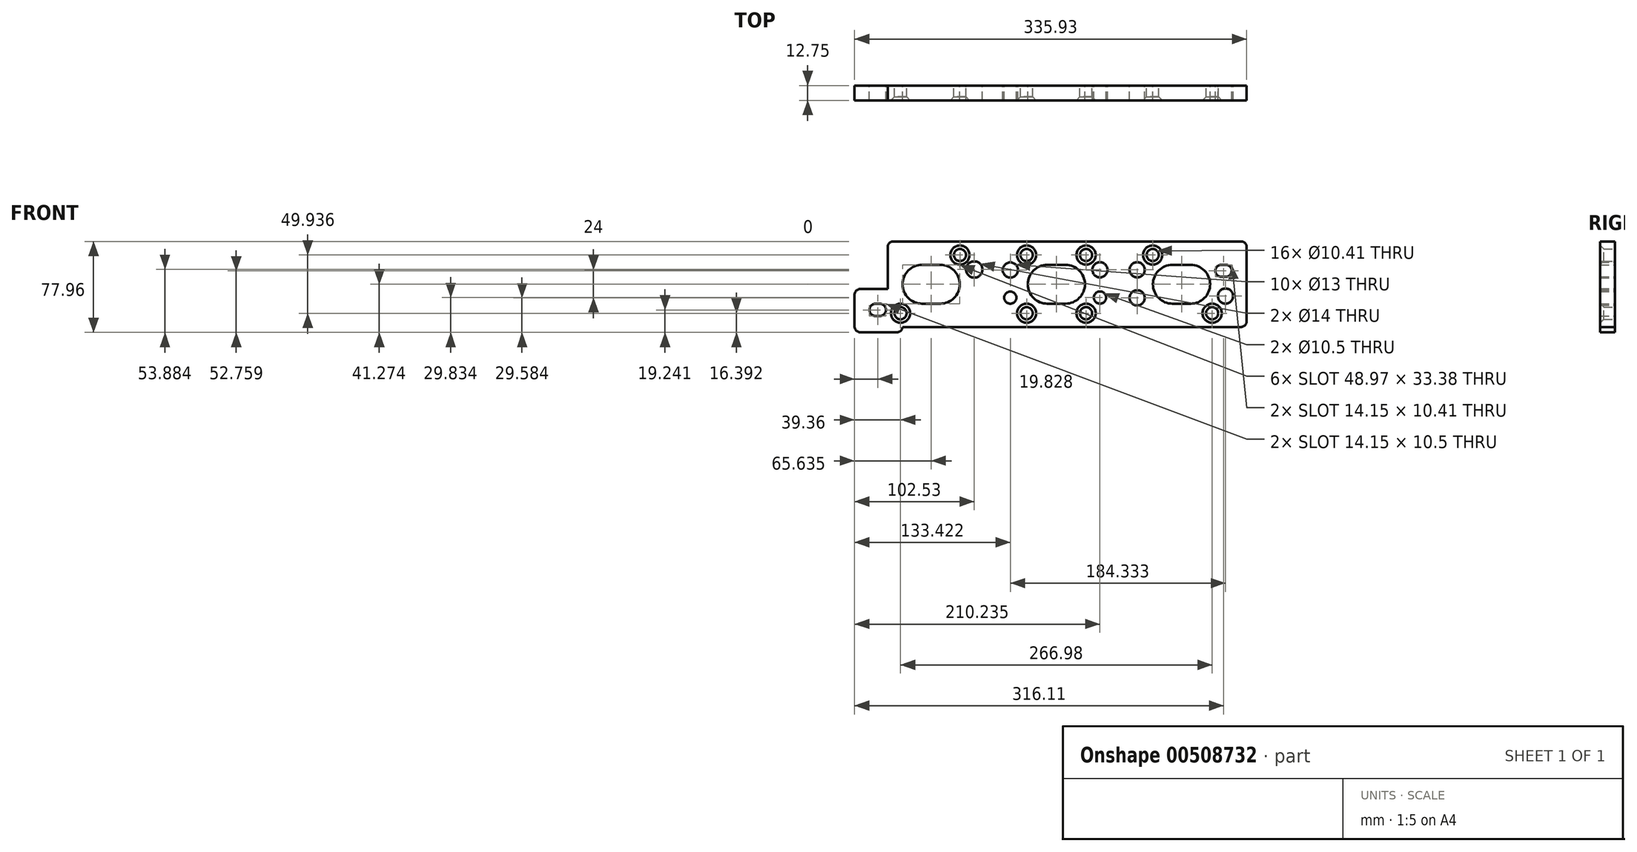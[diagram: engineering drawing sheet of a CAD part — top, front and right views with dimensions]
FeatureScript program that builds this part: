
annotation { "Feature Type Name" : "Feature", "Feature Type Description" : "" }
export const myFeature = defineFeature(function(context is Context, id is Id, definition is map)
    precondition{}
    {
        {
            var Q0;
            Q0=qCreatedBy(makeId("Front.planeOp"),FACE);
            var sketch = newSketch(context, id + "F0", { "sketchPlane" : qUnion([Q0])});
            skLineSegment(sketch, "E0", {"start": v(-7.76, 16.6) * mm, "end": v(7.83, 16.6) * mm});
            skArc(sketch, "E1", {"start": v(7.83, -16.78) * mm, "mid": v(24.52, -0.09) * mm, "end": v(7.83, 16.6) * mm});
            skLineSegment(sketch, "E2", {"start": v(7.83, -16.78) * mm, "end": v(-7.76, -16.78) * mm});
            skArc(sketch, "E3", {"start": v(-7.76, 16.6) * mm, "mid": v(-24.45, -0.09) * mm, "end": v(-7.76, -16.78) * mm});
            skPoint(sketch, "E4", {"position": v(-24.45, -0.09) * mm});
            skPoint(sketch, "E5", {"position": v(24.52, -0.09) * mm});
            skLineSegment(sketch, "E6", {"start": v(99.45, 16.6) * mm, "end": v(115.04, 16.6) * mm});
            skArc(sketch, "E7", {"start": v(115.04, -16.78) * mm, "mid": v(131.73, -0.09) * mm, "end": v(115.04, 16.6) * mm});
            skLineSegment(sketch, "E8", {"start": v(115.04, -16.78) * mm, "end": v(99.45, -16.78) * mm});
            skArc(sketch, "E9", {"start": v(99.45, 16.6) * mm, "mid": v(82.76, -0.09) * mm, "end": v(99.45, -16.78) * mm});
            skPoint(sketch, "E10", {"position": v(82.76, -0.09) * mm});
            skPoint(sketch, "E11", {"position": v(131.73, -0.09) * mm});
            skLineSegment(sketch, "E12", {"start": v(206.7, 16.6) * mm, "end": v(222.3, 16.6) * mm});
            skArc(sketch, "E13", {"start": v(222.3, -16.78) * mm, "mid": v(238.99, -0.09) * mm, "end": v(222.3, 16.6) * mm});
            skLineSegment(sketch, "E14", {"start": v(222.3, -16.78) * mm, "end": v(206.7, -16.78) * mm});
            skArc(sketch, "E15", {"start": v(206.7, 16.6) * mm, "mid": v(190.02, -0.09) * mm, "end": v(206.7, -16.78) * mm});
            skPoint(sketch, "E16", {"position": v(190.01, -0.09) * mm});
            skPoint(sketch, "E17", {"position": v(238.99, -0.09) * mm});
            skPoint(sketch, "E18", {"position": v(107.25, 0) * mm});
            skPoint(sketch, "E19", {"position": v(214.5, 0) * mm});
            skCircle(sketch, "E20", {"center": v(36.93, 12.52) * mm, "radius": 7 * mm});
            skCircle(sketch, "E21", {"center": v(67.82, 12.16) * mm, "radius": 6.5 * mm});
            skCircle(sketch, "E22", {"center": v(67.82, -11.58) * mm, "radius": 5.2 * mm});
            skPoint(sketch, "E23", {"position": v(67.82, -16.78) * mm});
            skLineSegment(sketch, "E24", {"start": v(-47.6, -16.87) * mm, "end": v(-43.95, -16.87) * mm});
            skArc(sketch, "E25", {"start": v(-43.95, -27.37) * mm, "mid": v(-38.7, -22.12) * mm, "end": v(-43.95, -16.87) * mm});
            skLineSegment(sketch, "E26", {"start": v(-43.95, -27.37) * mm, "end": v(-47.6, -27.37) * mm});
            skArc(sketch, "E27", {"start": v(-47.6, -16.87) * mm, "mid": v(-52.85, -22.12) * mm, "end": v(-47.6, -27.37) * mm});
            skPoint(sketch, "E28", {"position": v(-38.7, -22.12) * mm});
            skPoint(sketch, "E29", {"position": v(-52.85, -22.12) * mm});
            skCircle(sketch, "E30", {"center": v(144.63, 12.22) * mm, "radius": 6.5 * mm});
            skCircle(sketch, "E31", {"center": v(144.63, -11.53) * mm, "radius": 5.25 * mm});
            skPoint(sketch, "E32", {"position": v(144.63, -16.78) * mm});
            skPoint(sketch, "E33", {"position": v(138.13, 12.22) * mm});
            skCircle(sketch, "E34", {"center": v(176.51, 12.22) * mm, "radius": 6.5 * mm});
            skCircle(sketch, "E35", {"center": v(176.51, -11.78) * mm, "radius": 6.5 * mm});
            skPoint(sketch, "E36", {"position": v(183.01, 12.22) * mm});
            skLineSegment(sketch, "E37", {"start": v(248.64, 16.6) * mm, "end": v(252.38, 16.6) * mm});
            skArc(sketch, "E38", {"start": v(252.38, 6.2) * mm, "mid": v(257.59, 11.4) * mm, "end": v(252.38, 16.6) * mm});
            skLineSegment(sketch, "E39", {"start": v(252.38, 6.2) * mm, "end": v(248.64, 6.2) * mm});
            skArc(sketch, "E40", {"start": v(248.64, 16.6) * mm, "mid": v(243.44, 11.4) * mm, "end": v(248.64, 6.2) * mm});
            skPoint(sketch, "E41", {"position": v(243.44, 11.4) * mm});
            skPoint(sketch, "E42", {"position": v(257.59, 11.4) * mm});
            skCircle(sketch, "E43", {"center": v(252.16, -10.28) * mm, "radius": 6.5 * mm});
            skPoint(sketch, "E44", {"position": v(252.16, -16.78) * mm});
            skPoint(sketch, "E45", {"position": v(245.65, -10.28) * mm});
            skSolve(sketch);
        }
        {
            var Q0;
            Q0=qCreatedBy(makeId("Front.planeOp"),FACE);
            var sketch = newSketch(context, id + "F1", { "sketchPlane" : qUnion([Q0])});
            skLineSegment(sketch, "E46", {"start": v(-37.2, 36.6) * mm, "end": v(270.33, 36.6) * mm});
            skLineSegment(sketch, "E47", {"start": v(270.33, 36.6) * mm, "end": v(270.33, -36.78) * mm});
            skLineSegment(sketch, "E48", {"start": v(270.33, -36.78) * mm, "end": v(-24.45, -36.78) * mm});
            skLineSegment(sketch, "E49", {"start": v(-24.45, -36.78) * mm, "end": v(-24.45, -41.36) * mm});
            skLineSegment(sketch, "E50", {"start": v(-24.45, -41.36) * mm, "end": v(-65.6, -41.36) * mm});
            skLineSegment(sketch, "E51", {"start": v(-65.6, -41.36) * mm, "end": v(-65.6, -4.12) * mm});
            skLineSegment(sketch, "E52", {"start": v(-65.6, -4.12) * mm, "end": v(-37.2, -4.12) * mm});
            skLineSegment(sketch, "E53", {"start": v(-37.2, -4.12) * mm, "end": v(-37.2, 36.6) * mm});
            skLineSegment(sketch, "E54", {"start": v(-37.2, 36.6) * mm, "end": v(-37.2, 36.6) * mm});
            skSolve(sketch);
        }
        {
            var Q0;
            Q0 = qSketchRegion(id + "F1", true);
            extrude(context, id + "F2", {"entities" : qUnion([Q0]), "depth" : 12.75 * mm});
        }
        {
            var Q0;
            Q0 = qSketchRegion(id + "F0", true);
            extrude(context, id + "F3", {"entities" : qUnion([Q0]), "operationType" : NewBodyOperationType.REMOVE, "depth" : 25 * mm});
        }
        {
            var Q0;
            Q0=makeQuery(id+"F2.opExtrude","SWEPT_EDGE",EDGE,{"disambiguationData":[OSD([sQuery(id+"F1.wireOp",EDGE,"E46"),sQuery(id+"F1.wireOp",EDGE,"E53")])]});
            var Q1;
            Q1=makeQuery(id+"F2.opExtrude","SWEPT_EDGE",EDGE,{"disambiguationData":[OSD([sQuery(id+"F1.wireOp",EDGE,"E51"),sQuery(id+"F1.wireOp",EDGE,"E52")])]});
            var Q2;
            Q2=makeQuery(id+"F2.opExtrude","SWEPT_EDGE",EDGE,{"disambiguationData":[OSD([sQuery(id+"F1.wireOp",EDGE,"E50"),sQuery(id+"F1.wireOp",EDGE,"E51")])]});
            var Q3;
            Q3=makeQuery(id+"F2.opExtrude","SWEPT_EDGE",EDGE,{"disambiguationData":[OSD([sQuery(id+"F1.wireOp",EDGE,"E49"),sQuery(id+"F1.wireOp",EDGE,"E50")])]});
            var Q4;
            Q4=makeQuery(id+"F2.opExtrude","SWEPT_EDGE",EDGE,{"disambiguationData":[OSD([sQuery(id+"F1.wireOp",EDGE,"E46"),sQuery(id+"F1.wireOp",EDGE,"E47")])]});
            var Q5;
            Q5=makeQuery(id+"F2.opExtrude","SWEPT_EDGE",EDGE,{"disambiguationData":[OSD([sQuery(id+"F1.wireOp",EDGE,"E47"),sQuery(id+"F1.wireOp",EDGE,"E48")])]});
            fillet(context, id + "F4", {"entities" : qUnion([Q0, Q1, Q2, Q3, Q4, Q5]), "radius" : 5 * mm, "tangentPropagation" : true, "allowEdgeOverflow" : false});
        }
        {
            var Q0;
            Q0=qCreatedBy(makeId("Front.planeOp"),FACE);
            var sketch = newSketch(context, id + "F5", { "sketchPlane" : qUnion([Q0])});
            skCircle(sketch, "E55", {"center": v(132.71, 24.97) * mm, "radius": 5.2 * mm});
            skCircle(sketch, "E56", {"center": v(132.71, -24.97) * mm, "radius": 5.2 * mm});
            skCircle(sketch, "E57", {"center": v(81.79, -24.97) * mm, "radius": 5.2 * mm});
            skCircle(sketch, "E58", {"center": v(81.79, 24.97) * mm, "radius": 5.2 * mm});
            skCircle(sketch, "E59", {"center": v(240.74, -24.97) * mm, "radius": 5.2 * mm});
            skCircle(sketch, "E60", {"center": v(-26.24, -24.97) * mm, "radius": 5.2 * mm});
            skCircle(sketch, "E61", {"center": v(24.69, 24.97) * mm, "radius": 5.2 * mm});
            skCircle(sketch, "E62", {"center": v(189.81, 24.97) * mm, "radius": 5.2 * mm});
            skSolve(sketch);
        }
        {
            var Q0;
            Q0 = qSketchRegion(id + "F5", true);
            extrude(context, id + "F6", {"entities" : qUnion([Q0]), "operationType" : NewBodyOperationType.REMOVE, "depth" : 25 * mm});
        }
        {
            var Q0;
            Q0=makeQuery(id+"F6.boolean.opBoolean","INTERSECT",EDGE,{"derivedFrom":[makeQuery(id+"F2.opExtrude","CAP_FACE",FACE,{"disambiguationData":[OSD([sQuery(id+"F1.wireOp",EDGE,"E46"),sQuery(id+"F1.wireOp",EDGE,"E47"),sQuery(id+"F1.wireOp",EDGE,"E48"),sQuery(id+"F1.wireOp",EDGE,"E49"),sQuery(id+"F1.wireOp",EDGE,"E50"),sQuery(id+"F1.wireOp",EDGE,"E51"),sQuery(id+"F1.wireOp",EDGE,"E52"),sQuery(id+"F1.wireOp",EDGE,"E53")])],"isStart":false}),makeQuery(id+"F6.opExtrude","SWEPT_FACE",FACE,{"disambiguationData":[OSD([sQuery(id+"F5.wireOp",EDGE,"E61")])]})]});
            var Q1;
            Q1=makeQuery(id+"F6.boolean.opBoolean","INTERSECT",EDGE,{"derivedFrom":[makeQuery(id+"F2.opExtrude","CAP_FACE",FACE,{"disambiguationData":[OSD([sQuery(id+"F1.wireOp",EDGE,"E46"),sQuery(id+"F1.wireOp",EDGE,"E47"),sQuery(id+"F1.wireOp",EDGE,"E48"),sQuery(id+"F1.wireOp",EDGE,"E49"),sQuery(id+"F1.wireOp",EDGE,"E50"),sQuery(id+"F1.wireOp",EDGE,"E51"),sQuery(id+"F1.wireOp",EDGE,"E52"),sQuery(id+"F1.wireOp",EDGE,"E53")])],"isStart":false}),makeQuery(id+"F6.opExtrude","SWEPT_FACE",FACE,{"disambiguationData":[OSD([sQuery(id+"F5.wireOp",EDGE,"E60")])]})]});
            var Q2;
            Q2=makeQuery(id+"F6.boolean.opBoolean","INTERSECT",EDGE,{"derivedFrom":[makeQuery(id+"F2.opExtrude","CAP_FACE",FACE,{"disambiguationData":[OSD([sQuery(id+"F1.wireOp",EDGE,"E46"),sQuery(id+"F1.wireOp",EDGE,"E47"),sQuery(id+"F1.wireOp",EDGE,"E48"),sQuery(id+"F1.wireOp",EDGE,"E49"),sQuery(id+"F1.wireOp",EDGE,"E50"),sQuery(id+"F1.wireOp",EDGE,"E51"),sQuery(id+"F1.wireOp",EDGE,"E52"),sQuery(id+"F1.wireOp",EDGE,"E53")])],"isStart":false}),makeQuery(id+"F6.opExtrude","SWEPT_FACE",FACE,{"disambiguationData":[OSD([sQuery(id+"F5.wireOp",EDGE,"E58")])]})]});
            var Q3;
            Q3=makeQuery(id+"F6.boolean.opBoolean","INTERSECT",EDGE,{"derivedFrom":[makeQuery(id+"F2.opExtrude","CAP_FACE",FACE,{"disambiguationData":[OSD([sQuery(id+"F1.wireOp",EDGE,"E46"),sQuery(id+"F1.wireOp",EDGE,"E47"),sQuery(id+"F1.wireOp",EDGE,"E48"),sQuery(id+"F1.wireOp",EDGE,"E49"),sQuery(id+"F1.wireOp",EDGE,"E50"),sQuery(id+"F1.wireOp",EDGE,"E51"),sQuery(id+"F1.wireOp",EDGE,"E52"),sQuery(id+"F1.wireOp",EDGE,"E53")])],"isStart":false}),makeQuery(id+"F6.opExtrude","SWEPT_FACE",FACE,{"disambiguationData":[OSD([sQuery(id+"F5.wireOp",EDGE,"E55")])]})]});
            var Q4;
            Q4=makeQuery(id+"F6.boolean.opBoolean","INTERSECT",EDGE,{"derivedFrom":[makeQuery(id+"F2.opExtrude","CAP_FACE",FACE,{"disambiguationData":[OSD([sQuery(id+"F1.wireOp",EDGE,"E46"),sQuery(id+"F1.wireOp",EDGE,"E47"),sQuery(id+"F1.wireOp",EDGE,"E48"),sQuery(id+"F1.wireOp",EDGE,"E49"),sQuery(id+"F1.wireOp",EDGE,"E50"),sQuery(id+"F1.wireOp",EDGE,"E51"),sQuery(id+"F1.wireOp",EDGE,"E52"),sQuery(id+"F1.wireOp",EDGE,"E53")])],"isStart":false}),makeQuery(id+"F6.opExtrude","SWEPT_FACE",FACE,{"disambiguationData":[OSD([sQuery(id+"F5.wireOp",EDGE,"E56")])]})]});
            var Q5;
            Q5=makeQuery(id+"F6.boolean.opBoolean","INTERSECT",EDGE,{"derivedFrom":[makeQuery(id+"F2.opExtrude","CAP_FACE",FACE,{"disambiguationData":[OSD([sQuery(id+"F1.wireOp",EDGE,"E46"),sQuery(id+"F1.wireOp",EDGE,"E47"),sQuery(id+"F1.wireOp",EDGE,"E48"),sQuery(id+"F1.wireOp",EDGE,"E49"),sQuery(id+"F1.wireOp",EDGE,"E50"),sQuery(id+"F1.wireOp",EDGE,"E51"),sQuery(id+"F1.wireOp",EDGE,"E52"),sQuery(id+"F1.wireOp",EDGE,"E53")])],"isStart":false}),makeQuery(id+"F6.opExtrude","SWEPT_FACE",FACE,{"disambiguationData":[OSD([sQuery(id+"F5.wireOp",EDGE,"E57")])]})]});
            var Q6;
            Q6=makeQuery(id+"F6.boolean.opBoolean","INTERSECT",EDGE,{"derivedFrom":[makeQuery(id+"F2.opExtrude","CAP_FACE",FACE,{"disambiguationData":[OSD([sQuery(id+"F1.wireOp",EDGE,"E46"),sQuery(id+"F1.wireOp",EDGE,"E47"),sQuery(id+"F1.wireOp",EDGE,"E48"),sQuery(id+"F1.wireOp",EDGE,"E49"),sQuery(id+"F1.wireOp",EDGE,"E50"),sQuery(id+"F1.wireOp",EDGE,"E51"),sQuery(id+"F1.wireOp",EDGE,"E52"),sQuery(id+"F1.wireOp",EDGE,"E53")])],"isStart":false}),makeQuery(id+"F6.opExtrude","SWEPT_FACE",FACE,{"disambiguationData":[OSD([sQuery(id+"F5.wireOp",EDGE,"E62")])]})]});
            var Q7;
            Q7=makeQuery(id+"F6.boolean.opBoolean","INTERSECT",EDGE,{"derivedFrom":[makeQuery(id+"F2.opExtrude","CAP_FACE",FACE,{"disambiguationData":[OSD([sQuery(id+"F1.wireOp",EDGE,"E46"),sQuery(id+"F1.wireOp",EDGE,"E47"),sQuery(id+"F1.wireOp",EDGE,"E48"),sQuery(id+"F1.wireOp",EDGE,"E49"),sQuery(id+"F1.wireOp",EDGE,"E50"),sQuery(id+"F1.wireOp",EDGE,"E51"),sQuery(id+"F1.wireOp",EDGE,"E52"),sQuery(id+"F1.wireOp",EDGE,"E53")])],"isStart":false}),makeQuery(id+"F6.opExtrude","SWEPT_FACE",FACE,{"disambiguationData":[OSD([sQuery(id+"F5.wireOp",EDGE,"E59")])]})]});
            chamfer(context, id + "F7", {"entities" : qUnion([Q0, Q1, Q2, Q3, Q4, Q5, Q6, Q7]), "width" : 3 * mm, "tangentPropagation" : true});
        }
    });
